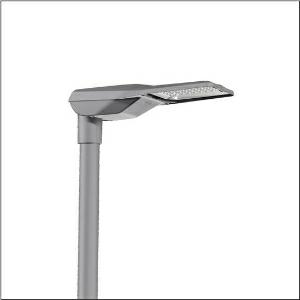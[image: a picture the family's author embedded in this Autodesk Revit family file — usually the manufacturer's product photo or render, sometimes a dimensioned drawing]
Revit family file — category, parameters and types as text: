
# Revit family: streetlight_sl_21_iq_mini___stw1_0a_5xe2e41g08jb_4c9f
name_source: partatom
category: Lighting Fixtures
units: mm (PartAtom-declared; Revit-internal decimal feet)

## family parameters
Cut with Voids When Loaded = No
Host = Face
Light Source = No
Part Type = Normal
Room Calculation Point = No
Round Connector Dimension = Use Diameter
Shared = No

## types (1)
- --- (1 x LED, 11290 lm, 71.6 W, 4000K)
    Apparent Load = 72 VA
    CIE Flux Codes = 39 75 98 100 100
    Color Rendering = 70
    Color Temperature = 4000K
    Default Elevation = 1800 mm
    Description = Streetlight SL 21 iQ mini, mast luminaire, primary light control with lens, of PMMA, primary optical cover: cover, of toughened safety glass, transparent, light distribution: STW1.0a, light emission: direct distribution, primary light characteristic: asymmetric, installation type: post-top, side-entry, LED, High Power LED, rated luminous flux: 11.290lm, luminous efficacy: 158lm/W, light colour: 740, colour temperature: 4000K, control gear: iQ Street-Remote, control: Street-Remote, Auto-Match, Temp-Guard, Lumen-Switch, Night-Set, Smart-Wire, Light-Fading, Desk-Remote (wireless, voltage-free reading and setting of iQ features in the workshop via application-optimized NFC function/RFID function), optimised constant luminous flux control (CLO 2.0), pre-setting: linear dimming characteristic, mains connection: 220..240V, AC, 50/60Hz, start of lifetime: 72W, end of service life: 75W, reduction: 33W, luminaire housing, of diecast aluminium, powder-coated, SITECO metallic grey (DB 702S), corrosivity category C5 high according to DIN EN ISO 12944, please order mast flange separately, inclination adjustable: 0°, 5°, 10°, 15°, sealing non-destructively replaceable, multi-level sealing system, length: 628mm, width: 235mm, height: 110mm, mast flange for spigot size: 42mm (side-entry): 5XC10008XM4, 60/48mm (side-entry/post-top): 5XC10108XM2, 76/60mm (side-entry/post-top): 5XC10108XM1, mounting height: 4..8m, protection rating (complete): IP66, insulation class (complete): insulation class II (safety insulation), certification: CE, ENEC, ENEC+, VDE, impact resistance: IK10, permissible operating ambient temperature for outdoor applications: -40..+50°C, standard-compliant lighting for roads and squares, packaging unit: 1 piece

Light Distribution: STW1.0a
    Height = 110 mm
    Lamp = 1 x LED
    Lamp Light Flux = 11290 lm
    Lamp Power = 71.6 W
    Lamp count = 1
    Length = 625 mm
    Luminous efficacy = 158 lm/W
    Manufacturer = Siteco
    ModVariant = No
    Model = 5XE2E41G08JB
    Number of Poles = 1
    OnlyDefault = Yes
    Power Factor = 1
    Product Name = Streetlight SL 21 iQ mini | STW1.0a
    Product group = mast luminaire | pylon top
    ProductGroupID = 6100
    Protection Class = Protection class II
    Protection Degree = IP 66
    RLX_Detail_Level = 1
    RLX_Emergency_Light_Flux = 0 lm
    RLX_Emergency_Type = 0
    RLX_Emergency_Type_DB = No
    RlxData = <blob elided: 26381 chars, md5=9aa8fc74>
    Socket = socket
    Standby Power = 0 W
    System Light Flux = 11290 lm
    System Power = 72 W
    Type Comments = factory setting: luminous flux: 100 % | dim-lin: 254 | 746 mA
    Type Image = l_1003519.jpg
    URL = http://relux.com
    VarID = @adj_169597
    Voltage = 0 V
    Weight = 0.00 kg
    Width = 234 mm

## geometry (parser evidence)
native form markers: Blend x4, Sweep x11
no freeform markers — native parametric forms only
